SOLIDWORKS PART (.sldprt)
format: sldprt  version: not decoded by parser v0  size: 3,933,696 bytes
history: native  units: mm
features: sketch x26, plane x9, material x1, extrude x1, pattern_circular x1 (+15 scaffold rows collapsed)
feature tree (53):
  scaffold x15  (default folders/planes/origin — collapsed)
  material  "A36"
  sketch  "Sketch1"  dims[D1=~225.775067mm]
  sketch  "Sketch2"  dims[D1=~225.775067mm]
  sketch  "Sketch3"
  sketch  "Sketch4"
  sketch  "Sketch5"
  sketch  "Sketch9"
  sketch  "Sketch10"
  sketch  "Sketch11"
  sketch  "Sketch12"
  sketch  "Sketch13"
  plane  "Plane1"
  plane  "Plane2"
  plane  "Plane3"
  plane  "Plane4"
  plane  "Plane5"
  plane  "Plane6"
  plane  "Plane7"
  plane  "Plane8"
  plane  "Plane9"
  sketch  "Sketch21"  dims[D1=76.2mm]
  sketch  "Sketch22"
  sketch  "3DSketch6"  dims[D1=0.0mm]
  sketch  "Sketch6"
  sketch  "Sketch7"
  sketch  "Sketch8"
  sketch  "Sketch14"
  sketch  "Sketch15"
  sketch  "Sketch16"
  sketch  "Sketch17"
  sketch  "Sketch18"
  sketch  "3DSketch4"
  sketch  "3DSketch5"
  sketch  "3DSketch7"
  sketch  "3DSketch8"
  sketch  "Sketch23"
  extrude  "Extrude1"  [1 undecoded]
  pattern_circular  "CirPattern1"  Count=2 Angle=360deg Thickness=4.7625mm
decode coverage: 5 of 28 modeling features carry decoded parameters
note: ~ marks probable driven/reference dimensions
note: 1 parameter value undecoded
note: suppression state not decoded; provenance and decode notes live in map.json
